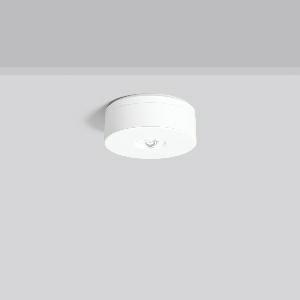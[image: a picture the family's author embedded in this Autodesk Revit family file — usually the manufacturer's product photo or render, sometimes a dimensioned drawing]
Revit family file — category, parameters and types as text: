
# Revit family: lucio_2_672527_002_171e
name_source: partatom
category: Lighting Fixtures
units: mm (PartAtom-declared; Revit-internal decimal feet)

## family parameters
Cut with Voids When Loaded = No
Host = Face
Light Source = No
Part Type = Normal
Room Calculation Point = No
Round Connector Dimension = Use Diameter
Shared = No

## types (1)
- Flaechenlinse 3h (1 x LED Modul 740, 240 lm, 4000)
    Apparent Load = 0 VA
    CIE Flux Codes = 45 88 99 100 100
    Color Rendering = 70
    Color Temperature = 4000
    Default Elevation = 1800 mm
    Description = Series: LUCIO 2
Round surface-mounted downlight. For escape route illumination. Housing: plastic (polycarbonate). Cover: polycarbonate. Plastic lenses for area lighting and escape route illumination included in scope of delivery. Suitable for Ceiling mounting. Electronic ballast included. Self-contained system with automatic self-test. 
Colour: white
Diameter: 110 mm
Height: 46 mm
Weight: 0.28 kg
Operating mode: non-maintained power mode
Duration time: 3 h, 8 h
Lamp: LED
Socket: without socket
Colour temperature: 4000K
Colour rendering index (CRI): 70
Luminous flux, emergency: 240 lm
System power, emergency: -
Luminous flux, emergency 2: 240 lm
System power, emergency 2: -
Luminous flux, emergency 3: 120 lm
System power, emergency 3: -
Luminous flux, emergency 4: 120 lm
Control gear: EB in emergency mode only
Protection class: II
Type of protection: IP 20
    Height = 46 mm
    Lamp = 1 x LED Modul 740
    Lamp Light Flux = 240 lm
    Lamp count = 1
    Length = 110 mm
    Lifetime = 50000 h
    Luminous efficacy = 0 lm/W
    Manufacturer = RZB
    ModVariant = No
    Model = 672527.002
    Mounting Place = Ceiling
    Mounting Type = Surface mounted
    Number of Poles = 1
    OnlyDefault = Yes
    Power Factor = 1
    Product Name = LUCIO 2
    Product group = Surface mounted ceiling luminaires
    ProductGroupID = 303
    Protection Class = Protection class II
    Protection Degree = Degree of protection
    RLX_Detail_Level = 1
    RLX_Emergency_Light_Flux = 240 lm
    RLX_Emergency_Type = 3
    RLX_Emergency_Type_DB = Yes
    RlxData = <blob elided: 196337 chars, md5=ef6015e1>
    Socket = socket
    Standby Power = 0 W
    System Light Flux = 0 lm
    System Power = 0 W
    Type Image = 672527.002.jpg
    URL = http://relux.com
    VarID = flaechenlinse_3h
    Voltage = 0 V
    Weight = 0.00 kg
    Width = 0 mm  [stored 0 ft]

note: [stored X ft] marks values corroborated as IEEE doubles in the binary element streams (Revit-internal decimal feet)

## geometry (parser evidence)
native form markers: Blend x4, Sweep x9
no freeform markers — native parametric forms only
